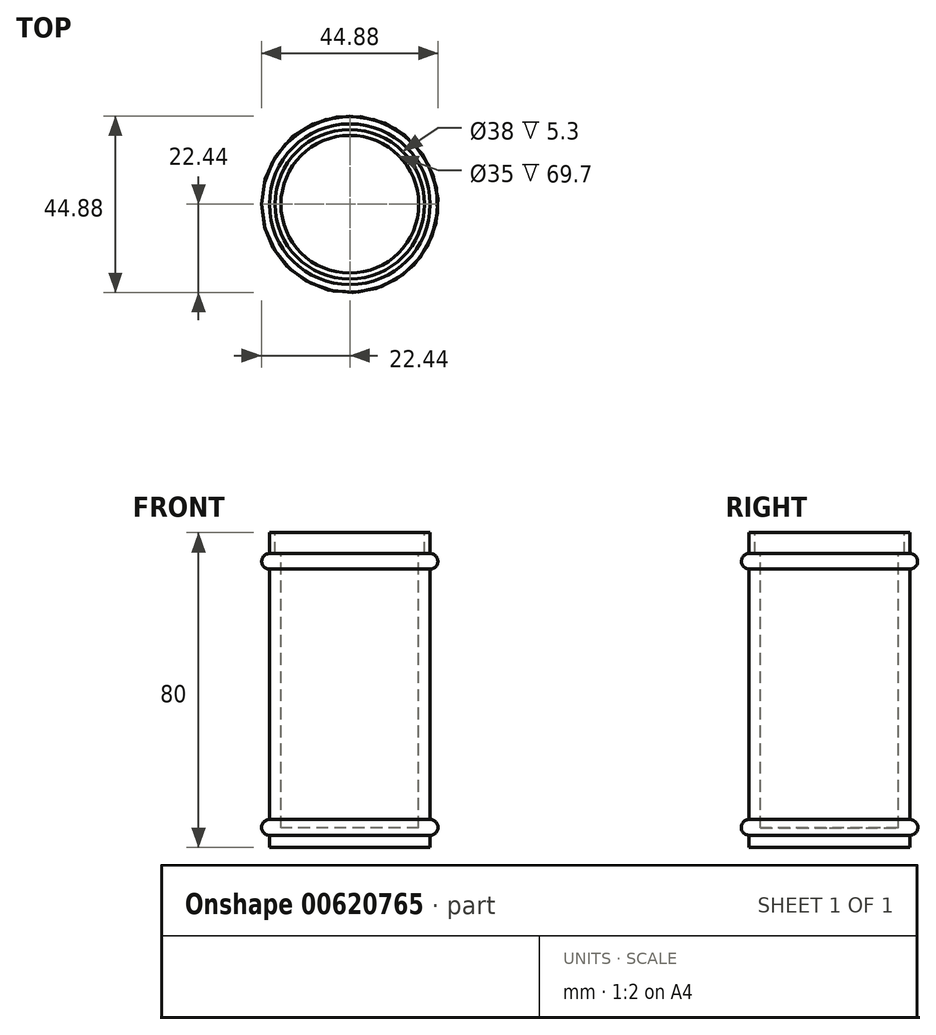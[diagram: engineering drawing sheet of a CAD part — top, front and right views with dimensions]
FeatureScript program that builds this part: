
annotation { "Feature Type Name" : "Feature", "Feature Type Description" : "" }
export const myFeature = defineFeature(function(context is Context, id is Id, definition is map)
    precondition{}
    {
        {
            var Q0;
            Q0=qCreatedBy(makeId("Top.planeOp"),FACE);
            var sketch = newSketch(context, id + "F0", { "sketchPlane" : qUnion([Q0])});
            skCircle(sketch, "E0", {"center": v(0, 0) * mm, "radius": 20.42 * mm});
            skSolve(sketch);
        }
        {
            var Q0;
            Q0=makeQuery(id+"F0.imprint","IMPRINT",FACE,{"disambiguationData":[TD([[makeQuery(id+"F0.imprint","IMPRINT",EDGE,{"derivedFrom":sQuery(id+"F0.wireOp",EDGE,"E0")}),1.0]])]});
            extrude(context, id + "F1", {"entities" : qUnion([Q0]), "depth" : 80 * mm, "offsetDistance" : 25 * mm});
        }
        {
            var Q0;
            Q0=makeQuery(id+"F1.opExtrude","CAP_FACE",FACE,{"disambiguationData":[OSD([sQuery(id+"F0.wireOp",EDGE,"E0")])],"isStart":false});
            var sketch = newSketch(context, id + "F2", { "sketchPlane" : qUnion([Q0])});
            skCircle(sketch, "E1", {"center": v(0, 0) * mm, "radius": 17.5 * mm});
            skSolve(sketch);
        }
        {
            var Q0;
            Q0 = qSketchRegion(id + "F2", true);
            extrude(context, id + "F3", {"entities" : qUnion([Q0]), "operationType" : NewBodyOperationType.REMOVE, "oppositeDirection" : true, "depth" : 75 * mm, "offsetDistance" : 25 * mm});
        }
        {
            var Q0;
            Q0=makeQuery(id+"F2.imprint","IMPRINT",FACE,{"disambiguationData":[TD([[makeQuery(id+"F2.imprint","IMPRINT",EDGE,{"derivedFrom":sQuery(id+"F2.wireOp",EDGE,"E1")}),1.0]])]});
            var sketch = newSketch(context, id + "F4", { "sketchPlane" : qUnion([Q0])});
            skCircle(sketch, "E2", {"center": v(0, 0) * mm, "radius": 19 * mm});
            skSolve(sketch);
        }
        {
            var Q0;
            Q0 = qSketchRegion(id + "F4", true);
            extrude(context, id + "F5", {"entities" : qUnion([Q0]), "operationType" : NewBodyOperationType.REMOVE, "oppositeDirection" : true, "depth" : 5.3 * mm, "offsetDistance" : 25 * mm});
        }
        {
            var Q0;
            Q0=qCreatedBy(makeId("Right.planeOp"),FACE);
            var sketch = newSketch(context, id + "F6", { "sketchPlane" : qUnion([Q0])});
            skLineSegment(sketch, "E3", {"start": v(0, 0) * mm, "end": v(0, 84.96) * mm, "construction": true});
            skCircle(sketch, "E4", {"center": v(20.38, 72.73) * mm, "radius": 2 * mm});
            skCircle(sketch, "E5", {"center": v(20.44, 5.12) * mm, "radius": 2 * mm});
            skSolve(sketch);
        }
        {
            var Q0;
            Q0 = qSketchRegion(id + "F6", true);
            var Q1;
            Q1=sQuery(id+"F6.wireOp",EDGE,"E3");
            revolve(context, id + "F7", {"operationType" : NewBodyOperationType.ADD, "entities" : qUnion([Q0]), "axis" : qUnion([Q1]), "revolveType" : RevolveType.FULL});
        }
    });
